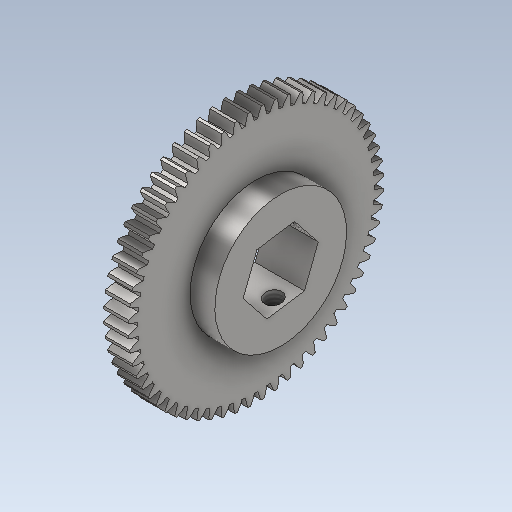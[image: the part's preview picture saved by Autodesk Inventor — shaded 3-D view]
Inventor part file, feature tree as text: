
AUTODESK INVENTOR PART (.ipt)
format: ipt  version: 2023 (Build 270158000, 158)  size: 1,091,072 bytes
history: native  units: in
note: dims shown in document units (in); Inventor stores cm internally (conversion verified against a paired STEP export)
features: sketch x3, extrude x1, revolve x1, hole x1, projected_geometry x1, other x1
ambient origin geometry x8: Origin, YZ Plane, XZ Plane, XY Plane, X Axis, Y Axis, Z Axis, Center Point
bodies: Solid1 (feature_tree)
feature tree (8):
  extrude  "Extrusion4"  Depth=0.1875in
  revolve  "Revolution1"  [1 undecoded]
  hole  "Hole2"  [1 undecoded]
  sketch  "Sketch6"  dims[d23=0.1875in d26=2.4724in]
  sketch  "Sketch7"  dims[d27=0.5in d28=0.0in d29=0.0in]
  sketch  "Sketch8"  dims[d30=0.5in d31=0.1875in d32=0.13in d33=0.328in d34=0.375in d35=0.25in d36=0.5635in d37=0.302in d38=0.8108in d39=0.0in d40=0.0in d41=0.0in d42=0.0in]
  projected_geometry  "Projected Loop1"
  other  "TeethCuts"
note: 2 required parameter values undecoded (feature->parameter linkage not recoverable at this tier; creation-order binding heuristic only, values carry confidence <= 0.55)